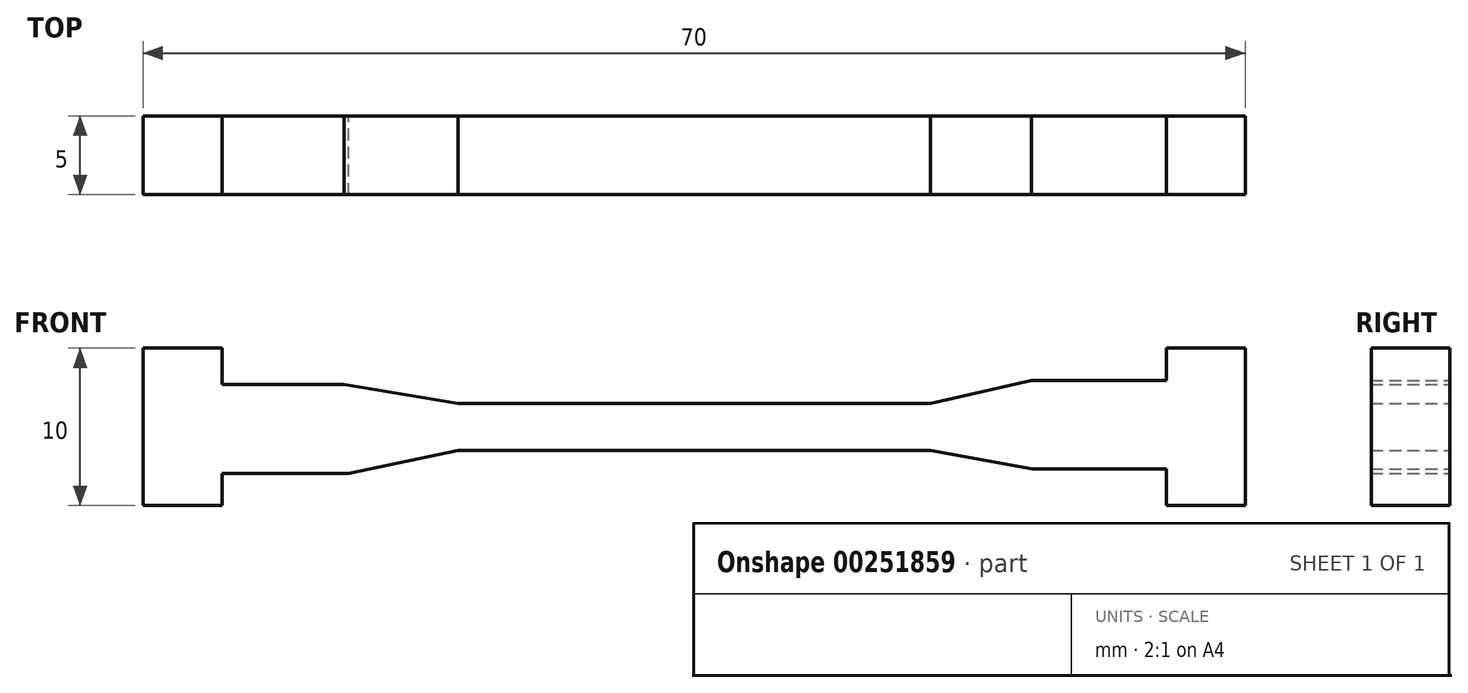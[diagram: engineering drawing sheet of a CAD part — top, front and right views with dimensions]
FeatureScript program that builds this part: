
annotation { "Feature Type Name" : "Feature", "Feature Type Description" : "" }
export const myFeature = defineFeature(function(context is Context, id is Id, definition is map)
    precondition{}
    {
        {
            var Q0;
            Q0=qCreatedBy(makeId("Front.planeOp"),FACE);
            var sketch = newSketch(context, id + "F0", { "sketchPlane" : qUnion([Q0])});
            skLineSegment(sketch, "E0.bottom", {"start": v(-35, 5) * mm, "end": v(-30, 5) * mm});
            skLineSegment(sketch, "E0.top", {"start": v(-35, -5) * mm, "end": v(-30, -5) * mm});
            skLineSegment(sketch, "E0.left", {"start": v(-35, 5) * mm, "end": v(-35, -5) * mm});
            skLineSegment(sketch, "E0.right", {"start": v(35, 5) * mm, "end": v(35, -5) * mm});
            skPoint(sketch, "E0.middle", {"position": v(0, 0) * mm});
            skLineSegment(sketch, "E1.left", {"start": v(-30, 5) * mm, "end": v(-30, 2.68) * mm});
            skLineSegment(sketch, "E1.right", {"start": v(30, 5) * mm, "end": v(30, 2.95) * mm});
            skLineSegment(sketch, "E2.bottom", {"start": v(-15, -1.5) * mm, "end": v(15, -1.5) * mm});
            skLineSegment(sketch, "E2.top", {"start": v(-15, 1.5) * mm, "end": v(15, 1.5) * mm});
            skLineSegment(sketch, "E3.trimOffspring", {"start": v(-30, -2.95) * mm, "end": v(-30, -5) * mm});
            skLineSegment(sketch, "E4.trimOffspring", {"start": v(30, -2.68) * mm, "end": v(30, -5) * mm});
            skLineSegment(sketch, "E5.trimOffspring", {"start": v(30, 5) * mm, "end": v(35, 5) * mm});
            skLineSegment(sketch, "E6.trimOffspring", {"start": v(30, -5) * mm, "end": v(35, -5) * mm});
            skLineSegment(sketch, "E7", {"start": v(30, -2.68) * mm, "end": v(21.48, -2.68) * mm});
            skLineSegment(sketch, "E8", {"start": v(30, 2.95) * mm, "end": v(21.43, 2.95) * mm});
            skLineSegment(sketch, "E9", {"start": v(-30, 2.68) * mm, "end": v(-22.23, 2.68) * mm});
            skLineSegment(sketch, "E10", {"start": v(-30, -2.95) * mm, "end": v(-21.96, -2.95) * mm});
            skLineSegment(sketch, "E11", {"start": v(21.48, -2.68) * mm, "end": v(21.48, -2.68) * mm});
            skLineSegment(sketch, "E12", {"start": v(-22.23, 2.68) * mm, "end": v(-15, 1.5) * mm});
            skLineSegment(sketch, "E13", {"start": v(-21.96, -2.95) * mm, "end": v(-15, -1.5) * mm});
            skLineSegment(sketch, "E14", {"start": v(15, 1.5) * mm, "end": v(21.43, 2.95) * mm});
            skLineSegment(sketch, "E15", {"start": v(15, -1.5) * mm, "end": v(21.48, -2.68) * mm});
            skSolve(sketch);
        }
        {
            var Q0;
            Q0 = qSketchRegion(id + "F0", true);
            extrude(context, id + "F1", {"entities" : qUnion([Q0]), "depth" : 5 * mm});
        }
    });
